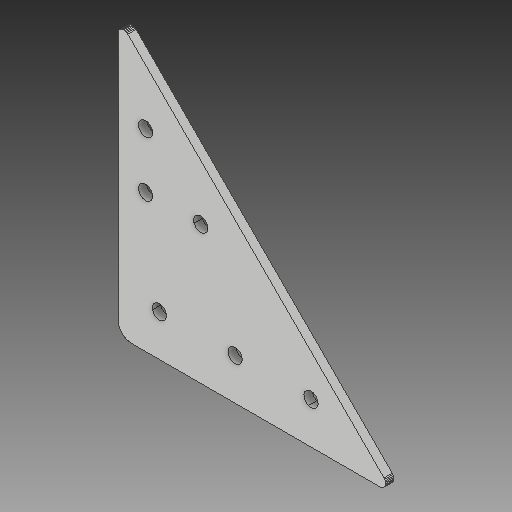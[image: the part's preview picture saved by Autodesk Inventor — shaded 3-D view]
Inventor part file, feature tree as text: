
AUTODESK INVENTOR PART (.ipt)
format: ipt  version: 2017 (Build 210142000, 142)  size: 209,408 bytes
history: native  units: mm
features: other x3, sketch x1
ambient origin geometry x8: Origin, YZ Plane, XZ Plane, XY Plane, X Axis, Y Axis, Z Axis, Center Point
bodies: Solid1 (feature_tree)
feature tree (4):
  other  "Side Brace_MIR.ipt"
  other  "Solid1::Side Brace_MIR.ipt"
  other  "TaggingFeature1"
  sketch  "Sketch1"  dims[d0=10.0mm]
